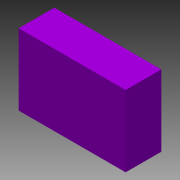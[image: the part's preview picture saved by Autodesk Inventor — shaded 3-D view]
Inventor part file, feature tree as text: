
AUTODESK INVENTOR PART (.ipt)
format: ipt  version: 2015 (Build 190159000, 159)  size: 81,408 bytes
history: native  units: in
note: dims shown in document units (in); Inventor stores cm internally (conversion verified against a paired STEP export)
features: extrude x1, sketch x1
ambient origin geometry x8: Origin, YZ Plane, XZ Plane, XY Plane, X Axis, Y Axis, Z Axis, Center Point
bodies: Solid1 (feature_tree)
feature tree (2):
  extrude  "Extrusion1"  Depth=2.25in
  sketch  "Sketch1"  dims[d0=1.5in d1=2.25in d2=0.75in d3=0.0in]
